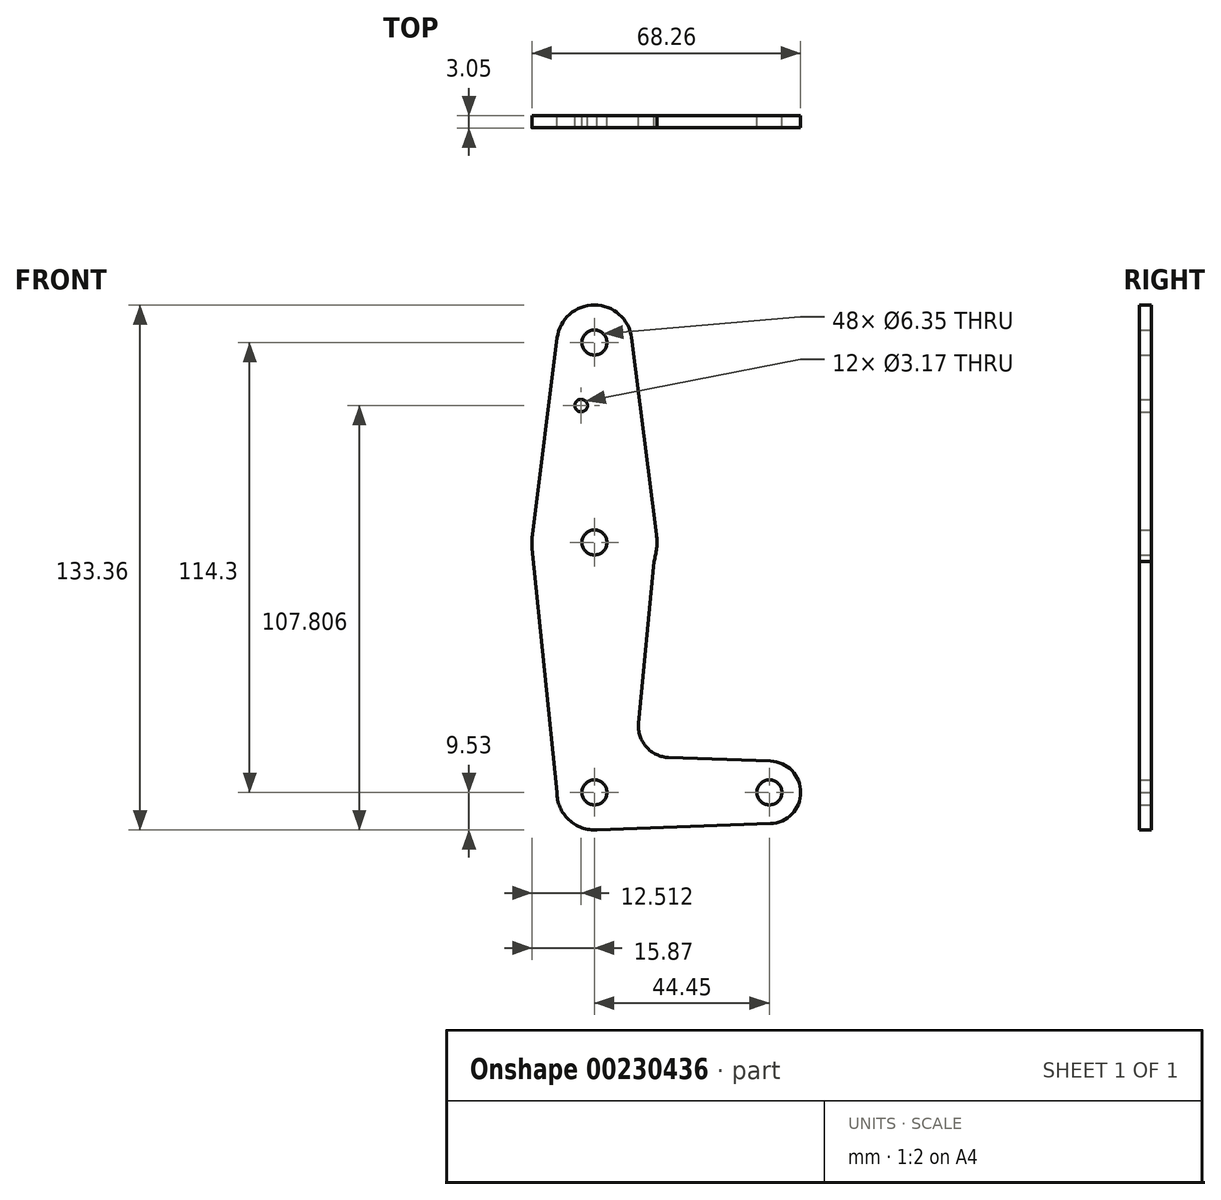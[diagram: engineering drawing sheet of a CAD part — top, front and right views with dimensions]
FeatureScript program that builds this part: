
annotation { "Feature Type Name" : "Feature", "Feature Type Description" : "" }
export const myFeature = defineFeature(function(context is Context, id is Id, definition is map)
    precondition{}
    {
        {
            var Q0;
            Q0=qCreatedBy(makeId("Front.planeOp"),FACE);
            var sketch = newSketch(context, id + "F0", { "sketchPlane" : qUnion([Q0])});
            skLineSegment(sketch, "E0", {"start": v(0, 0) * mm, "end": v(0, 63.5) * mm, "construction": true});
            skCircle(sketch, "E1", {"center": v(0, 63.5) * mm, "radius": 15.88 * mm});
            skCircle(sketch, "E2", {"center": v(0, 0) * mm, "radius": 9.53 * mm});
            skLineSegment(sketch, "E3", {"start": v(0, 0) * mm, "end": v(44.45, 0) * mm, "construction": true});
            skCircle(sketch, "E4", {"center": v(44.45, 0) * mm, "radius": 7.94 * mm});
            skLineSegment(sketch, "E5", {"start": v(0, 63.5) * mm, "end": v(0, 114.3) * mm, "construction": true});
            skCircle(sketch, "E6", {"center": v(0, 114.3) * mm, "radius": 9.53 * mm});
            skLineSegment(sketch, "E7", {"start": v(-9.45, 115.5) * mm, "end": v(-15.75, 65.48) * mm});
            skLineSegment(sketch, "E8", {"start": v(9.45, 115.5) * mm, "end": v(15.75, 65.48) * mm});
            skLineSegment(sketch, "E9", {"start": v(15.75, 65.48) * mm, "end": v(11.22, 17.55) * mm});
            skLineSegment(sketch, "E10", {"start": v(18.86, 8.85) * mm, "end": v(44.73, 7.93) * mm});
            skLineSegment(sketch, "E11", {"start": v(0, -9.53) * mm, "end": v(44.73, -7.93) * mm});
            skLineSegment(sketch, "E12", {"start": v(-9.53, 0) * mm, "end": v(-15.8, 61.9) * mm});
            skCircle(sketch, "E13", {"center": v(-3.36, 98.28) * mm, "radius": 1.59 * mm});
            skCircle(sketch, "E14", {"center": v(0, 114.3) * mm, "radius": 3.18 * mm});
            skCircle(sketch, "E15", {"center": v(0, 63.5) * mm, "radius": 3.18 * mm});
            skCircle(sketch, "E16", {"center": v(0, 0) * mm, "radius": 3.18 * mm});
            skCircle(sketch, "E17", {"center": v(44.45, 0) * mm, "radius": 3.18 * mm});
            skArc(sketch, "E18.filletArc", {"start": v(11.22, 17.55) * mm, "mid": v(13.16, 11.55) * mm, "end": v(18.86, 8.85) * mm});
            skSolve(sketch);
        }
        {
            var Q0;
            Q0 = qSketchRegion(id + "F0", true);
            extrude(context, id + "F1", {"entities" : qUnion([Q0]), "depth" : 3.05 * mm});
        }
        {
            var Q0;
            Q0 = qSketchRegion(id + "F0", true);
            extrude(context, id + "F2", {"entities" : qUnion([Q0]), "depth" : 3.05 * mm});
        }
    });
